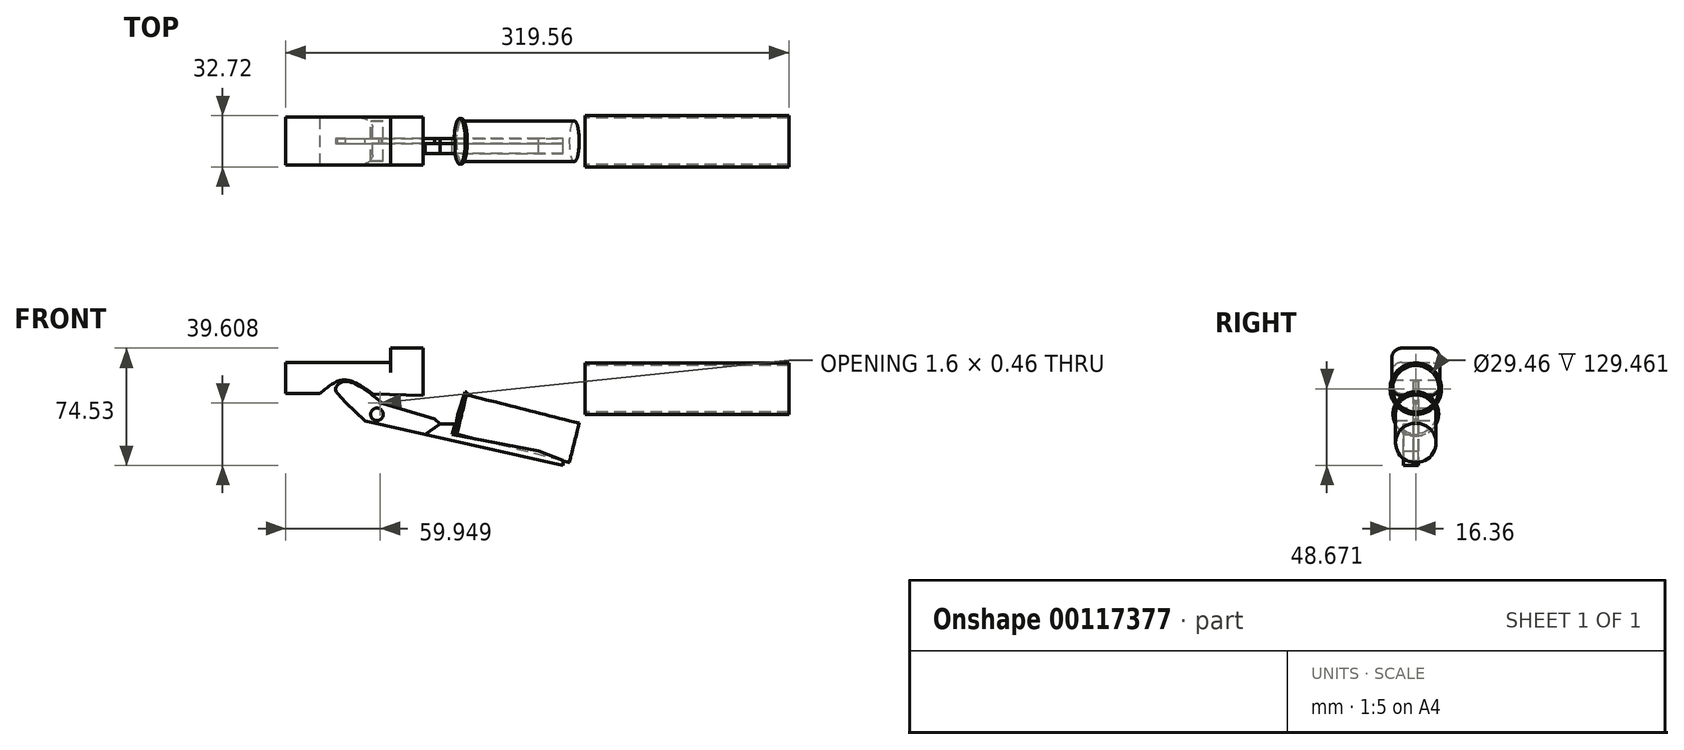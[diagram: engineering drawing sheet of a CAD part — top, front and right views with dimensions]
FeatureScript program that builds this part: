
annotation { "Feature Type Name" : "Feature", "Feature Type Description" : "" }
export const myFeature = defineFeature(function(context is Context, id is Id, definition is map)
    precondition{}
    {
        {
            var Q0;
            Q0=qCreatedBy(makeId("Front.planeOp"),FACE);
            var sketch = newSketch(context, id + "F0", { "sketchPlane" : qUnion([Q0])});
            skLineSegment(sketch, "E0", {"start": v(140.92, 99.13) * mm, "end": v(214.8, 80.5) * mm});
            skCircle(sketch, "E1", {"center": v(89.5, 98.62) * mm, "radius": 3.97 * mm});
            skArc(sketch, "E2", {"start": v(92.9, 91.94) * mm, "mid": v(91.14, 105.93) * mm, "end": v(83.58, 94.03) * mm});
            skCircle(sketch, "E3", {"center": v(69.24, 115.14) * mm, "radius": 3.07 * mm});
            skLineSegment(sketch, "E4", {"start": v(81.96, 94.4) * mm, "end": v(207.8, 66.17) * mm});
            skLineSegment(sketch, "E5", {"start": v(207.8, 66.17) * mm, "end": v(207.8, 72.35) * mm});
            skLineSegment(sketch, "E6", {"start": v(207.8, 72.35) * mm, "end": v(137.2, 85.9) * mm});
            skLineSegment(sketch, "E7", {"start": v(129.72, 92.59) * mm, "end": v(126.11, 95.81) * mm});
            skLineSegment(sketch, "E8", {"start": v(126.11, 95.81) * mm, "end": v(90.77, 106) * mm});
            skLineSegment(sketch, "E9", {"start": v(88.24, 106) * mm, "end": v(69.66, 106) * mm});
            skLineSegment(sketch, "E10", {"start": v(69.66, 106) * mm, "end": v(81.96, 94.4) * mm});
            skLineSegment(sketch, "E11", {"start": v(69.66, 106) * mm, "end": v(64.5, 111.74) * mm});
            skFitSpline(sketch, "E12", {"points": [v(64.5, 111.74) * mm, v(63.35, 114.47) * mm, v(66.24, 118.68) * mm, v(75.08, 118.35) * mm, v(90.76, 107.45) * mm], "startDerivative": vector(-11.77, 16.3) * mm, "endDerivative": vector(41.62, -34.55) * mm});
            skLineSegment(sketch, "E13", {"start": v(90.76, 107.45) * mm, "end": v(93.03, 105.36) * mm});
            skLineSegment(sketch, "E14", {"start": v(137.2, 85.9) * mm, "end": v(139.08, 92.59) * mm});
            skLineSegment(sketch, "E15", {"start": v(139.08, 92.59) * mm, "end": v(129.72, 92.59) * mm});
            skLineSegment(sketch, "E16", {"start": v(216.8, 64.54) * mm, "end": v(444.96, 50.45) * mm});
            skLineSegment(sketch, "E17", {"start": v(207.8, 69.26) * mm, "end": v(192.28, 75.33) * mm});
            skLineSegment(sketch, "E18", {"start": v(214.8, 80.5) * mm, "end": v(217.96, 92.98) * mm});
            skLineSegment(sketch, "E19", {"start": v(217.96, 92.98) * mm, "end": v(146.37, 111.05) * mm});
            skLineSegment(sketch, "E20", {"start": v(140.92, 99.13) * mm, "end": v(145.63, 112.91) * mm});
            skLineSegment(sketch, "E21", {"start": v(145.63, 112.91) * mm, "end": v(146.86, 112.5) * mm});
            skLineSegment(sketch, "E22", {"start": v(146.86, 112.5) * mm, "end": v(146.37, 111.05) * mm});
            skLineSegment(sketch, "E23", {"start": v(118.95, 110.45) * mm, "end": v(118.95, 140.7) * mm});
            skLineSegment(sketch, "E24", {"start": v(118.95, 140.7) * mm, "end": v(98.15, 140.7) * mm});
            skLineSegment(sketch, "E25", {"start": v(98.15, 140.7) * mm, "end": v(98.15, 131.6) * mm});
            skLineSegment(sketch, "E26", {"start": v(98.15, 131.6) * mm, "end": v(31.62, 131.6) * mm});
            skLineSegment(sketch, "E27", {"start": v(31.62, 131.6) * mm, "end": v(31.62, 112) * mm});
            skLineSegment(sketch, "E28", {"start": v(31.62, 112) * mm, "end": v(53.45, 112) * mm});
            skLineSegment(sketch, "E29", {"start": v(118.95, 110.45) * mm, "end": v(86.7, 111.65) * mm});
            skFitSpline(sketch, "E30", {"points": [v(53.45, 112) * mm, v(68.48, 120.42) * mm, v(86.7, 111.65) * mm], "startDerivative": vector(30.41, 25.8) * mm, "endDerivative": vector(36.01, -25.8) * mm});
            skLineSegment(sketch, "E31.bottom", {"start": v(221.72, 100.1) * mm, "end": v(351.18, 100.1) * mm});
            skLineSegment(sketch, "E31.top", {"start": v(221.72, 98.48) * mm, "end": v(351.18, 98.48) * mm});
            skLineSegment(sketch, "E31.left", {"start": v(221.72, 100.1) * mm, "end": v(221.72, 98.48) * mm});
            skLineSegment(sketch, "E31.right", {"start": v(351.18, 100.1) * mm, "end": v(351.18, 98.48) * mm});
            skLineSegment(sketch, "E32", {"start": v(221.72, 100.1) * mm, "end": v(221.72, 114.84) * mm});
            skLineSegment(sketch, "E33", {"start": v(221.72, 114.84) * mm, "end": v(236.85, 114.84) * mm});
            skLineSegment(sketch, "E34", {"start": v(61.98, 144.12) * mm, "end": v(61.98, 131.6) * mm});
            skLineSegment(sketch, "E35", {"start": v(31.62, 131.6) * mm, "end": v(38.44, 147.98) * mm});
            skArc(sketch, "E36", {"start": v(38.44, 147.98) * mm, "mid": v(49.94, 144.4) * mm, "end": v(61.98, 144.12) * mm});
            skLineSegment(sketch, "E37", {"start": v(219.34, 137.17) * mm, "end": v(160.8, 142.45) * mm});
            skLineSegment(sketch, "E38", {"start": v(160.8, 142.45) * mm, "end": v(143.71, 152) * mm});
            skLineSegment(sketch, "E39", {"start": v(143.71, 152) * mm, "end": v(139.83, 145.04) * mm});
            skLineSegment(sketch, "E40", {"start": v(139.83, 145.04) * mm, "end": v(127.2, 145.04) * mm});
            skLineSegment(sketch, "E41", {"start": v(127.2, 145.04) * mm, "end": v(123.62, 141.24) * mm});
            skLineSegment(sketch, "E42", {"start": v(123.62, 141.24) * mm, "end": v(44, 145.8) * mm});
            skLineSegment(sketch, "E43", {"start": v(44, 145.8) * mm, "end": v(44, 152.58) * mm});
            skSolve(sketch);
        }
        {
            var Q0;
            Q0=makeQuery(id+"F0.imprint","IMPRINT",FACE,{"disambiguationData":[TD([[makeQuery(id+"F0.imprint","IMPRINT",EDGE,{"derivedFrom":sQuery(id+"F0.wireOp",EDGE,"E23")}),1.0]])]});
            extrude(context, id + "F1", {"entities" : qUnion([Q0]), "endBound" : BoundingType.SYMMETRIC, "depth" : 30.48 * mm});
        }
        {
            var Q0;
            {var subQ10=sQuery(id+"F0.wireOp",EDGE,"E7");Q0=makeQuery(id+"F0.imprint","IMPRINT",FACE,{"disambiguationData":[TD([[makeQuery(id+"F0.imprint","IMPRINT",EDGE,{"derivedFrom":subQ10}),1.0]])]});}
            var Q1;
            Q1=makeQuery(id+"F0.imprint","IMPRINT",FACE,{"disambiguationData":[TD([[makeQuery(id+"F0.imprint","IMPRINT",EDGE,{"derivedFrom":sQuery(id+"F0.wireOp",EDGE,"E1")}),-1.0]])]});
            var Q2;
            {var subQ3=sQuery(id+"F0.wireOp",EDGE,"E9");Q2=makeQuery(id+"F0.imprint","IMPRINT",FACE,{"disambiguationData":[TD([[makeQuery(id+"F0.imprint","IMPRINT",EDGE,{"derivedFrom":subQ3}),1.0]])]});}
            var Q3;
            Q3=makeQuery(id+"F0.imprint","IMPRINT",FACE,{"disambiguationData":[TD([[makeQuery(id+"F0.imprint","IMPRINT",EDGE,{"derivedFrom":sQuery(id+"F0.wireOp",EDGE,"E3")}),-1.0]])]});
            extrude(context, id + "F2", {"entities" : qUnion([Q0, Q1, Q2, Q3]), "endBound" : BoundingType.SYMMETRIC, "depth" : 3.17 * mm});
        }
        {
            var Q0;
            Q0=makeQuery(id+"F0.imprint","IMPRINT",FACE,{"disambiguationData":[TD([[makeQuery(id+"F0.imprint","IMPRINT",EDGE,{"derivedFrom":sQuery(id+"F0.wireOp",EDGE,"E1")}),1.0]])]});
            extrude(context, id + "F3", {"entities" : qUnion([Q0]), "operationType" : NewBodyOperationType.ADD, "endBound" : BoundingType.SYMMETRIC, "depth" : 25.4 * mm});
        }
        {
            var Q0;
            Q0=makeQuery(id+"F0.imprint","IMPRINT",FACE,{"disambiguationData":[TD([[makeQuery(id+"F0.imprint","IMPRINT",EDGE,{"derivedFrom":sQuery(id+"F0.wireOp",EDGE,"E3")}),1.0]])]});
            extrude(context, id + "F4", {"entities" : qUnion([Q0]), "operationType" : NewBodyOperationType.ADD, "endBound" : BoundingType.SYMMETRIC, "depth" : 3.17 * mm});
        }
        {
            var Q0;
            Q0=makeQuery(id+"F1.opExtrude","CAP_EDGE",EDGE,{"disambiguationData":[OSD([sQuery(id+"F0.wireOp",EDGE,"E24")])],"isStart":false});
            var Q1;
            Q1=makeQuery(id+"F1.opExtrude","CAP_EDGE",EDGE,{"disambiguationData":[OSD([sQuery(id+"F0.wireOp",EDGE,"E24")])],"isStart":true});
            var Q2;
            Q2=makeQuery(id+"F1.opExtrude","CAP_EDGE",EDGE,{"disambiguationData":[OSD([sQuery(id+"F0.wireOp",EDGE,"E26")])],"isStart":false});
            var Q3;
            Q3=makeQuery(id+"F1.opExtrude","CAP_EDGE",EDGE,{"disambiguationData":[OSD([sQuery(id+"F0.wireOp",EDGE,"E26")])],"isStart":true});
            var Q4;
            Q4=makeQuery(id+"F1.opExtrude","CAP_EDGE",EDGE,{"disambiguationData":[OSD([sQuery(id+"F0.wireOp",EDGE,"E29")])],"isStart":false});
            var Q5;
            Q5=makeQuery(id+"F1.opExtrude","CAP_EDGE",EDGE,{"disambiguationData":[OSD([sQuery(id+"F0.wireOp",EDGE,"E29")])],"isStart":true});
            fillet(context, id + "F5", {"entities" : qUnion([Q0, Q1, Q2, Q3, Q4, Q5]), "radius" : 6.35 * mm, "tangentPropagation" : true, "allowEdgeOverflow" : false});
        }
        {
            var Q0;
            {var subQ0=sQuery(id+"F0.wireOp",EDGE,"E3");Q0=makeQuery(id+"F4.boolean.opBoolean","MERGE",FACE,{"derivedFrom":[makeQuery(id+"F2.opExtrude","CAP_FACE",FACE,{"disambiguationData":[OSD([sQuery(id+"F0.wireOp",EDGE,"E1"),sQuery(id+"F0.wireOp",EDGE,"E2"),subQ0,sQuery(id+"F0.wireOp",EDGE,"E4"),sQuery(id+"F0.wireOp",EDGE,"E5"),sQuery(id+"F0.wireOp",EDGE,"E6"),sQuery(id+"F0.wireOp",EDGE,"E7"),sQuery(id+"F0.wireOp",EDGE,"E8"),sQuery(id+"F0.wireOp",EDGE,"E10"),sQuery(id+"F0.wireOp",EDGE,"E11"),sQuery(id+"F0.wireOp",EDGE,"E12"),sQuery(id+"F0.wireOp",EDGE,"E13"),sQuery(id+"F0.wireOp",EDGE,"E14"),sQuery(id+"F0.wireOp",EDGE,"E15"),sQuery(id+"F0.wireOp",EDGE,"E17")])],"isStart":false}),makeQuery(id+"F4.opExtrude","CAP_FACE",FACE,{"disambiguationData":[OSD([subQ0])],"isStart":false})]});}
            var sketch = newSketch(context, id + "F6", { "sketchPlane" : qUnion([Q0])});
            skLineSegment(sketch, "E44", {"start": v(129.72, 92.59) * mm, "end": v(120.1, 85.84) * mm});
            skSolve(sketch);
        }
        {
            var Q0;
            Q0 = qSketchRegion(id + "F6", true);
            var Q1;
            {var subQ2=sQuery(id+"F6.wireOp",EDGE,"E44");Q1=makeQuery(id+"F6.imprint","IMPRINT",FACE,{"disambiguationData":[TD([[makeQuery(id+"F6.imprint","IMPRINT",EDGE,{"derivedFrom":subQ2}),1.0]])]});}
            extrude(context, id + "F7", {"entities" : qUnion([Q0, Q1]), "depth" : 6.35 * mm});
        }
        {
            var Q0;
            Q0=makeQuery(id+"F0.imprint","IMPRINT",FACE,{"disambiguationData":[TD([[makeQuery(id+"F0.imprint","IMPRINT",EDGE,{"derivedFrom":sQuery(id+"F0.wireOp",EDGE,"E0")}),1.0]])]});
            var Q1;
            Q1=sQuery(id+"F0.wireOp",EDGE,"E0");
            revolve(context, id + "F8", {"entities" : qUnion([Q0]), "axis" : qUnion([Q1]), "revolveType" : RevolveType.FULL});
        }
        {
            var Q0;
            Q0=makeQuery(id+"F0.imprint","IMPRINT",FACE,{"disambiguationData":[TD([[makeQuery(id+"F0.imprint","IMPRINT",EDGE,{"derivedFrom":sQuery(id+"F0.wireOp",EDGE,"E31.bottom")}),-1.0]])]});
            var Q1;
            Q1=sQuery(id+"F0.wireOp",EDGE,"E33");
            revolve(context, id + "F9", {"entities" : qUnion([Q0]), "axis" : qUnion([Q1]), "revolveType" : RevolveType.FULL});
        }
    });
